# Revit family: Thorn PIAZZA II LED
name_source: partatom
category: Lighting Fixtures
revit_build: Autodesk Revit 2016 (Build: 20150220_1215(x64)
units: mm (PartAtom-declared; Revit-internal decimal feet)

## family parameters
Cut with Voids When Loaded = No
Host = Face
Light Source = Yes
OmniClass Number = 23.80.70.11
OmniClass Title = Luminaries for Internal Lighting
Part Type = Normal
Room Calculation Point = No
Round Connector Dimension = Use Diameter
Shared = No

## types (2) — shared parameters
Assembly Code = D5020210
Color Filter = 16777215
Description = LED luminaire
Dimming Lamp Color Temperature Shift = <None>
Height = 306 mm
Lamp = LED
Length = 383 mm
Manufacturer = Thorn Lighting
Tilt Angle = -90.00°
Voltage = 230 V
Width = 195 mm
zero-valued in all types: Versatz

## per-type parameters (varying)
| type | Apparent Load | Default Elevation | Model | Photometric Web File | URL |
| PIAZZA II LED 1690 | 15 VA | 2000 mm  [stored 6.56168 ft] | 96666256 | 96666256_(STD).IES | www.thornlighting.com/96666256 |
| PIAZZA II LED 2700 | 25 VA | 0 mm  [stored 0 ft] | 96666261 | 96666261_(STD).IES | www.thornlighting.com/96666261 |

note: [stored X ft] marks values corroborated as IEEE doubles in the binary element streams (Revit-internal decimal feet)

## geometry (parser evidence)
native form markers: Sweep x3
no freeform markers — native parametric forms only
